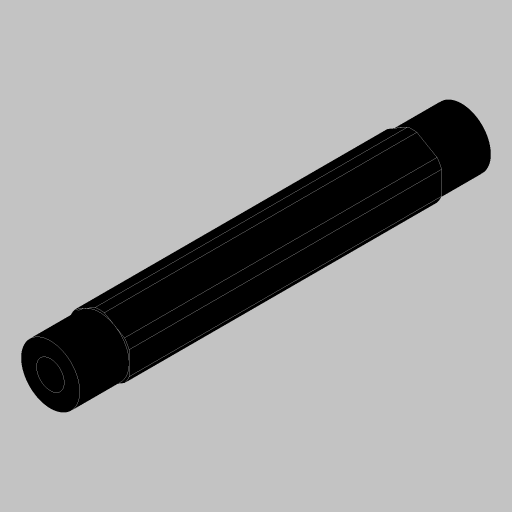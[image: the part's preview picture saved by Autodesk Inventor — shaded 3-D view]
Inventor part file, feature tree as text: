
AUTODESK INVENTOR PART (.ipt)
format: ipt  version: 2023.5 (Build 275446000, 446)  size: 163,840 bytes
history: native  units: in
note: dims shown in document units (in); Inventor stores cm internally (conversion verified against a paired STEP export)
features: extrude x3, projected_geometry x3, hole x1, mirror x1, sketch x1
ambient origin geometry x8: Origin, YZ Plane, XZ Plane, XY Plane, X Axis, Y Axis, Z Axis, Center Point
bodies: Solid1 (feature_tree)
feature tree (9):
  extrude  "Extrusion1"  Depth=0.315in
  hole  "Hole1"  [1 undecoded]
  extrude  "Extrusion3"  Depth=0.375in
  extrude  "Extrusion4"  Depth=0.315in TaperAngle=0.0deg
  mirror  "Mirror2"
  sketch  "Sketch5"  dims[d2=0.0in d9=0.625in d10=0.385in d11=0.25in d12=0.5635in d13=1.0in d14=0.8108in d16=0.7in d17=0.0in d18=0.0in d19=0.375in d20=0.315in d21=0.0in]
  projected_geometry  "Projected Loop2"
  projected_geometry  "Project Cut Edges1"
  projected_geometry  "Project Cut Edges2"
note: 1 required parameter value undecoded (feature->parameter linkage not recoverable at this tier; creation-order binding heuristic only, values carry confidence <= 0.55)
